# Revit family: 204_670c2b4e32d34831875dd830489997
name_source: partatom
category: Duct Accessories
revit_build: Autodesk Revit 2018 (Build: 20170223_1515(x64)
units: mm (PartAtom-declared; Revit-internal decimal feet)

## family parameters
Always vertical = Yes
Cut with Voids When Loaded = No
Part Type = Damper
Round Connector Dimension = Use Diameter
Shared = No
Work Plane-Based = No

## types (1)
- 03415
    C2 = 35 mm  [stored 0.114829 ft]
    D = 51 mm
    Description = Vacuum Cleaner Pipe collar for fire protection
    H2D = 51 mm  [stored 0.167323 ft]
    L2 = 1 mm  [stored 0.00328084 ft]
    L2D = 2 mm  [stored 0.00656168 ft]
    LT = 60 mm  [stored 0.19685 ft]
    LT2 = 30 mm  [stored 0.0984252 ft]
    MC Product Code = 03415
    MH = 70 mm  [stored 0.229659 ft]
    Manufacturer = Flexit
    QmdConnectorList = 201;D;202;D
    R = 26 mm
    URL = www.flexit.no
    W2D = 51 mm  [stored 0.167323 ft]
    Y = 35 mm  [stored 0.114829 ft]
    Z = 28 mm
    Z1 = 60 mm  [stored 0.19685 ft]
    magiPartTypeId = 204
    magiProductFamilyId = 670c2b4e32d34831875dd830489997
    magiProductId = 4455c6816be04338a266d9b3cb1ff3

note: [stored X ft] marks values corroborated as IEEE doubles in the binary element streams (Revit-internal decimal feet)

## geometry (parser evidence)
native form markers: Sweep x2
no freeform markers — native parametric forms only
